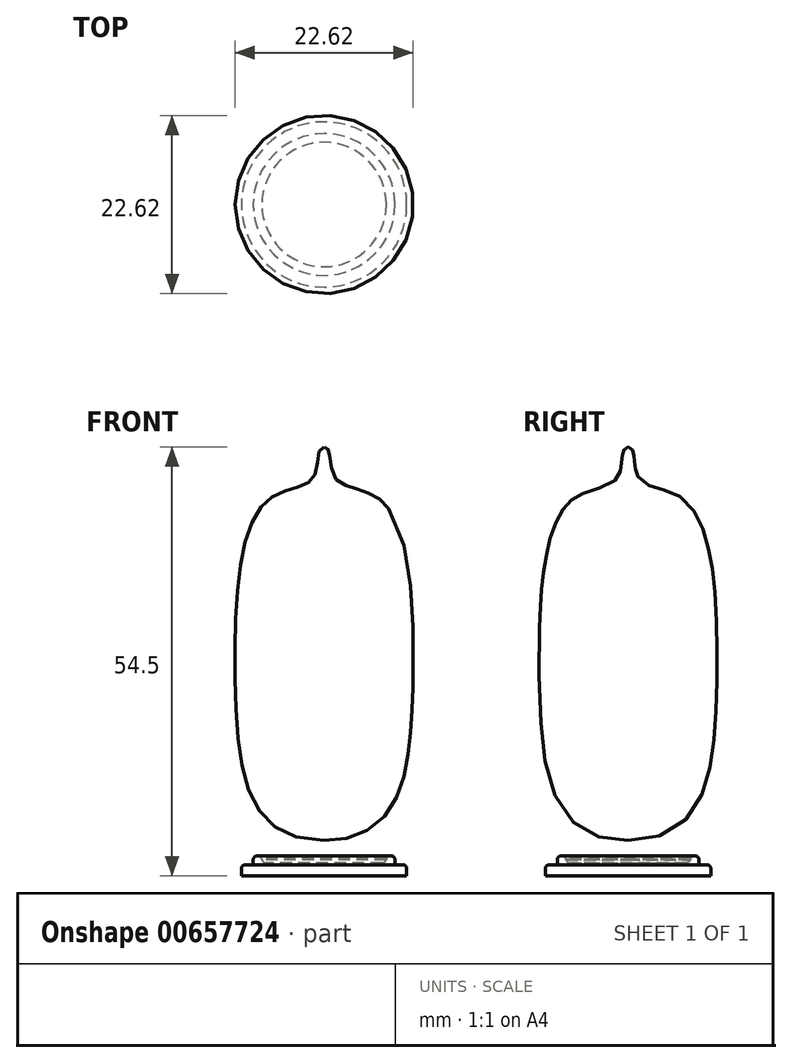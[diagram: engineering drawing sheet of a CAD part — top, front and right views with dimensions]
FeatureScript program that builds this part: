
annotation { "Feature Type Name" : "Feature", "Feature Type Description" : "" }
export const myFeature = defineFeature(function(context is Context, id is Id, definition is map)
    precondition{}
    {
        {
            var Q0;
            Q0=qCreatedBy(makeId("Front.planeOp"),FACE);
            var sketch = newSketch(context, id + "F0", { "sketchPlane" : qUnion([Q0])});
            skFitSpline(sketch, "E0", {"points": [v(0, 4.5) * mm, v(-11.25, 23.49) * mm, v(-7.2, 47.75) * mm, v(-1.25, 50.77) * mm, v(0, 54.5) * mm], "startDerivative": vector(-92.24, 0) * mm, "endDerivative": vector(22.57, -1.2) * mm});
            skLineSegment(sketch, "E1", {"start": v(0, 64.46) * mm, "end": v(0, -12.26) * mm});
            skLineSegment(sketch, "E2", {"start": v(0, 0) * mm, "end": v(-10.5, 0) * mm});
            skLineSegment(sketch, "E3", {"start": v(-10.5, 0) * mm, "end": v(-10.5, 0.94) * mm});
            skLineSegment(sketch, "E4", {"start": v(-10, 1.44) * mm, "end": v(-9, 1.44) * mm});
            skLineSegment(sketch, "E5", {"start": v(-9, 1.44) * mm, "end": v(-9, 2.07) * mm});
            skLineSegment(sketch, "E6", {"start": v(-8.5, 2.57) * mm, "end": v(-8.4, 2.57) * mm});
            skLineSegment(sketch, "E7", {"start": v(-7.9, 2.19) * mm, "end": v(-7.9, 2.07) * mm});
            skLineSegment(sketch, "E8", {"start": v(-7.4, 1.69) * mm, "end": v(0, 1.69) * mm});
            skPoint(sketch, "E9.visualSharp", {"position": v(-10.5, 1.44) * mm});
            skArc(sketch, "E9.filletArc", {"start": v(-10, 1.44) * mm, "mid": v(-10.35, 1.3) * mm, "end": v(-10.5, 0.94) * mm});
            skPoint(sketch, "E10.visualSharp", {"position": v(-9, 2.57) * mm});
            skArc(sketch, "E10.filletArc", {"start": v(-8.5, 2.57) * mm, "mid": v(-8.85, 2.42) * mm, "end": v(-9, 2.07) * mm});
            skPoint(sketch, "E11.visualSharp", {"position": v(-7.9, 2.57) * mm});
            skArc(sketch, "E11.filletArc", {"start": v(-7.9, 2.07) * mm, "mid": v(-8.05, 2.42) * mm, "end": v(-8.4, 2.57) * mm});
            skPoint(sketch, "E12.visualSharp", {"position": v(-7.9, 1.69) * mm});
            skArc(sketch, "E12.filletArc", {"start": v(-7.9, 2.19) * mm, "mid": v(-7.75, 1.83) * mm, "end": v(-7.4, 1.69) * mm});
            skSolve(sketch);
        }
        {
            var Q0;
            Q0 = qSketchRegion(id + "F0", true);
            var Q1;
            Q1=sQuery(id+"F0.wireOp",EDGE,"E1");
            revolve(context, id + "F1", {"entities" : qUnion([Q0]), "axis" : qUnion([Q1]), "revolveType" : RevolveType.FULL});
        }
    });
